annotation { "Feature Type Name" : "Feature", "Feature Type Description" : "" }
export const myFeature = defineFeature(function(context is Context, id is Id, definition is map)
    precondition{}
    {
        {
            var Q0;
            Q0=qCreatedBy(makeId("Right.planeOp"),FACE);
            var sketch = newSketch(context, id + "F0", { "sketchPlane" : qUnion([Q0])});
            skLineSegment(sketch, "E0", {"start": v(0, 0) * mm, "end": v(0, -25) * mm});
            skLineSegment(sketch, "E1", {"start": v(0, -25) * mm, "end": v(26.5, -25) * mm});
            skLineSegment(sketch, "E2", {"start": v(26.5, -25) * mm, "end": v(26.5, -25) * mm});
            skLineSegment(sketch, "E3", {"start": v(26.5, -25) * mm, "end": v(38.5, -25) * mm});
            skLineSegment(sketch, "E4.1", {"start": v(38.5, -30) * mm, "end": v(38.5, -25) * mm});
            skLineSegment(sketch, "E4.2", {"start": v(-5, -30) * mm, "end": v(38.5, -30) * mm});
            skLineSegment(sketch, "E4.3", {"start": v(-5, 0) * mm, "end": v(-5, -30) * mm});
            skLineSegment(sketch, "E5", {"start": v(-5, 0) * mm, "end": v(0, 0) * mm});
            skSolve(sketch);
        }
        {
            var Q0;
            Q0=makeQuery(id+"F0.imprint","IMPRINT",FACE,{"disambiguationData":[TD([[makeQuery(id+"F0.imprint","IMPRINT",EDGE,{"derivedFrom":sQuery(id+"F0.wireOp",EDGE,"E0")}),-1.0]])]});
            extrude(context, id + "F1", {"entities" : qUnion([Q0]), "depth" : 32 * mm, "offsetDistance" : 25 * mm});
        }
        {
            var Q0;
            Q0=makeQuery(id+"F1.opExtrude","SWEPT_FACE",FACE,{"disambiguationData":[OSD([sQuery(id+"F0.wireOp",EDGE,"E4.3")])]});
            var sketch = newSketch(context, id + "F2", { "sketchPlane" : qUnion([Q0])});
            skLineSegment(sketch, "E6.bottom", {"start": v(6.75, -8.25) * mm, "end": v(25.25, -8.25) * mm});
            skLineSegment(sketch, "E6.top", {"start": v(6.75, -11.75) * mm, "end": v(25.25, -11.75) * mm});
            skPoint(sketch, "E6.middle", {"position": v(16, -10) * mm});
            skPoint(sketch, "E6.middle.positionSnap0", {"position": v(16, 0) * mm});
            skPoint(sketch, "E6.centerSnap0", {"position": v(16, 0) * mm});
            skArc(sketch, "E7", {"start": v(25.25, -11.75) * mm, "mid": v(27, -10) * mm, "end": v(25.25, -8.25) * mm});
            skArc(sketch, "E8", {"start": v(6.75, -8.25) * mm, "mid": v(5, -10) * mm, "end": v(6.75, -11.75) * mm});
            skSolve(sketch);
        }
        {
            var Q0;
            Q0=makeQuery(id+"F2.imprint","IMPRINT",FACE,{"disambiguationData":[TD([[makeQuery(id+"F2.imprint","IMPRINT",EDGE,{"derivedFrom":sQuery(id+"F2.wireOp",EDGE,"E6.bottom")}),-1.0]])]});
            extrude(context, id + "F3", {"entities" : qUnion([Q0]), "operationType" : NewBodyOperationType.REMOVE, "endBound" : BoundingType.UP_TO_NEXT, "oppositeDirection" : true, "depth" : 25 * mm, "offsetDistance" : 25 * mm});
        }
        {
            var Q0;
            Q0=makeQuery(id+"F1.opExtrude","SWEPT_EDGE",EDGE,{"disambiguationData":[OSD([sQuery(id+"F0.wireOp",EDGE,"E4.2"),sQuery(id+"F0.wireOp",EDGE,"E4.3")])]});
            var Q1;
            Q1=makeQuery(id+"F1.opExtrude","SWEPT_EDGE",EDGE,{"disambiguationData":[OSD([sQuery(id+"F0.wireOp",EDGE,"E4.1"),sQuery(id+"F0.wireOp",EDGE,"E4.2")])]});
            var Q2;
            Q2=makeQuery(id+"F1.opExtrude","SWEPT_EDGE",EDGE,{"disambiguationData":[OSD([sQuery(id+"F0.wireOp",EDGE,"E4.3"),sQuery(id+"F0.wireOp",EDGE,"E5")])]});
            fillet(context, id + "F4", {"entities" : qUnion([Q0, Q1, Q2]), "radius" : 5 * mm, "tangentPropagation" : true, "allowEdgeOverflow" : false});
        }
        {
            var Q0;
            Q0=makeQuery(id+"F1.opExtrude","SWEPT_FACE",FACE,{"disambiguationData":[OSD([sQuery(id+"F0.wireOp",EDGE,"E4.2")])]});
            var sketch = newSketch(context, id + "F5", { "sketchPlane" : qUnion([Q0])});
            skPoint(sketch, "E9", {"position": v(16, -16.75) * mm});
            skPoint(sketch, "E9.positionSnap0", {"position": v(16, -33.5) * mm});
            skPoint(sketch, "E9.positionSnap1", {"position": v(0, -16.75) * mm});
            skText(sketch, "E10", { "text": "Nein Lara", "fontName": "RobotoSlab-Regular.ttf"});
            skLineSegment(sketch, "E11", {"start": v(32, -16.75) * mm, "end": v(0, -16.75) * mm, "construction": true});
            const initialGuessF5  = {"E10": [0.00986, -0.0024, 0.44517, -0.89545, 0.00538]};
            skSetInitialGuess(sketch, initialGuessF5);
            skSolve(sketch);
        }
        {
            var Q0;
            Q0 = qSketchRegion(id + "F5", true);
            extrude(context, id + "F6", {"entities" : qUnion([Q0]), "operationType" : NewBodyOperationType.REMOVE, "oppositeDirection" : true, "depth" : 0.2 * mm, "offsetDistance" : 25 * mm});
        }
        {
            var Q0;
            Q0=makeQuery(id+"F1.opExtrude","SWEPT_EDGE",EDGE,{"disambiguationData":[OSD([sQuery(id+"F0.wireOp",EDGE,"E0"),sQuery(id+"F0.wireOp",EDGE,"E1")])]});
            chamfer(context, id + "F7", {"entities" : qUnion([Q0]), "width" : 2 * mm, "tangentPropagation" : true});
        }
    });